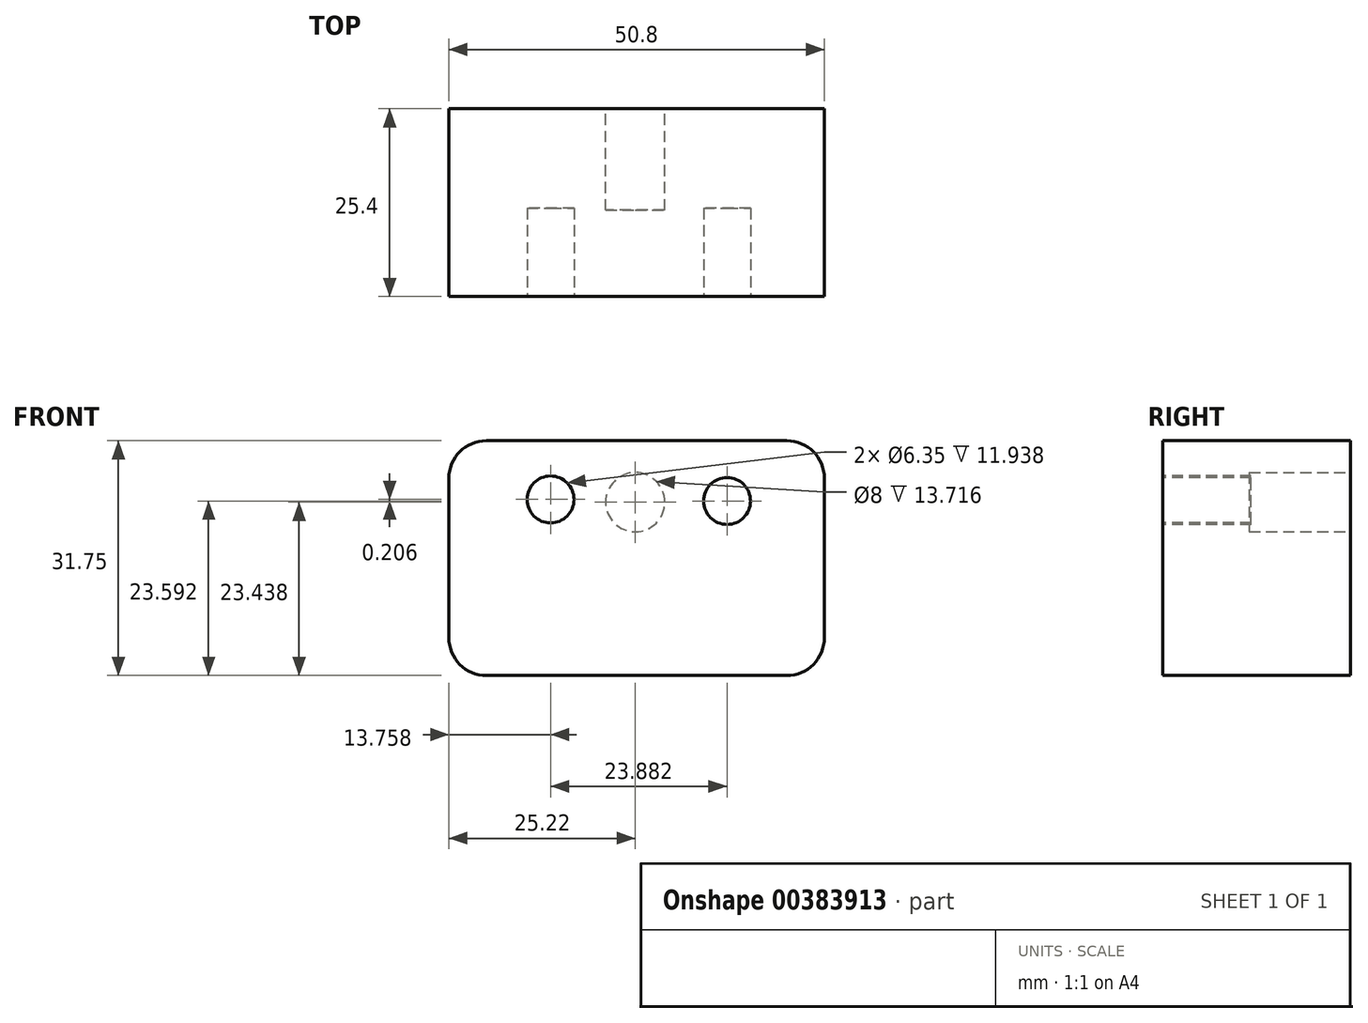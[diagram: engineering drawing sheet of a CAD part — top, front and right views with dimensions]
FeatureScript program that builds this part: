
annotation { "Feature Type Name" : "Feature", "Feature Type Description" : "" }
export const myFeature = defineFeature(function(context is Context, id is Id, definition is map)
    precondition{}
    {
        {
            var Q0;
            Q0=qCreatedBy(makeId("Top.planeOp"),FACE);
            var sketch = newSketch(context, id + "F0", { "sketchPlane" : qUnion([Q0])});
            skLineSegment(sketch, "E0.bottom", {"start": v(-25.22, 4.06) * mm, "end": v(25.58, 4.06) * mm});
            skLineSegment(sketch, "E0.top", {"start": v(-25.22, -21.34) * mm, "end": v(25.58, -21.34) * mm});
            skLineSegment(sketch, "E0.left", {"start": v(-25.22, 4.06) * mm, "end": v(-25.22, -21.34) * mm});
            skLineSegment(sketch, "E0.right", {"start": v(25.58, 4.06) * mm, "end": v(25.58, -21.34) * mm});
            skSolve(sketch);
        }
        {
            var Q0;
            Q0=makeQuery(id+"F0.imprint","IMPRINT",FACE,{"disambiguationData":[TD([[makeQuery(id+"F0.imprint","IMPRINT",EDGE,{"derivedFrom":sQuery(id+"F0.wireOp",EDGE,"E0.bottom")}),-1.0]])]});
            extrude(context, id + "F1", {"entities" : qUnion([Q0]), "depth" : 31.75 * mm});
        }
        {
            var Q0;
            Q0=makeQuery(id+"F1.opExtrude","SWEPT_FACE",FACE,{"disambiguationData":[OSD([sQuery(id+"F0.wireOp",EDGE,"E0.top")])]});
            var sketch = newSketch(context, id + "F2", { "sketchPlane" : qUnion([Q0])});
            skCircle(sketch, "E1", {"center": v(12.42, 23.6) * mm, "radius": 3.18 * mm});
            skCircle(sketch, "E2", {"center": v(-11.46, 23.8) * mm, "radius": 3.18 * mm});
            skSolve(sketch);
        }
        {
            var Q0;
            Q0=makeQuery(id+"F1.opExtrude","SWEPT_FACE",FACE,{"disambiguationData":[OSD([sQuery(id+"F0.wireOp",EDGE,"E0.bottom")])]});
            var sketch = newSketch(context, id + "F3", { "sketchPlane" : qUnion([Q0])});
            skCircle(sketch, "E3", {"center": v(0, 23.44) * mm, "radius": 4 * mm});
            skSolve(sketch);
        }
        {
            var Q0;
            Q0=makeQuery(id+"F3.imprint","IMPRINT",FACE,{"disambiguationData":[TD([[makeQuery(id+"F3.imprint","IMPRINT",EDGE,{"derivedFrom":sQuery(id+"F3.wireOp",EDGE,"E3")}),1.0]])]});
            extrude(context, id + "F4", {"entities" : qUnion([Q0]), "operationType" : NewBodyOperationType.REMOVE, "oppositeDirection" : true, "depth" : 13.72 * mm});
        }
        {
            var Q0;
            Q0=makeQuery(id+"F2.imprint","IMPRINT",FACE,{"disambiguationData":[TD([[makeQuery(id+"F2.imprint","IMPRINT",EDGE,{"derivedFrom":sQuery(id+"F2.wireOp",EDGE,"E2")}),1.0]])]});
            var Q1;
            Q1=makeQuery(id+"F2.imprint","IMPRINT",FACE,{"disambiguationData":[TD([[makeQuery(id+"F2.imprint","IMPRINT",EDGE,{"derivedFrom":sQuery(id+"F2.wireOp",EDGE,"E1")}),1.0]])]});
            extrude(context, id + "F5", {"entities" : qUnion([Q0, Q1]), "operationType" : NewBodyOperationType.REMOVE, "oppositeDirection" : true, "depth" : 11.94 * mm});
        }
        {
            var Q0;
            Q0=makeQuery(id+"F1.opExtrude","CAP_EDGE",EDGE,{"disambiguationData":[OSD([sQuery(id+"F0.wireOp",EDGE,"E0.left")])],"isStart":false});
            var Q1;
            Q1=makeQuery(id+"F1.opExtrude","CAP_EDGE",EDGE,{"disambiguationData":[OSD([sQuery(id+"F0.wireOp",EDGE,"E0.right")])],"isStart":false});
            var Q2;
            Q2=makeQuery(id+"F1.opExtrude","CAP_EDGE",EDGE,{"disambiguationData":[OSD([sQuery(id+"F0.wireOp",EDGE,"E0.right")])],"isStart":true});
            var Q3;
            Q3=makeQuery(id+"F1.opExtrude","CAP_EDGE",EDGE,{"disambiguationData":[OSD([sQuery(id+"F0.wireOp",EDGE,"E0.left")])],"isStart":true});
            fillet(context, id + "F6", {"entities" : qUnion([Q0, Q1, Q2, Q3]), "radius" : 5.08 * mm, "tangentPropagation" : true, "allowEdgeOverflow" : false});
        }
    });
